# Revit family: Domotics-DomesticRanges-GEWISS-27COMBI_SYSTEM-IP40_1P_2P_3P_4P
name_source: partatom
category: Apparecchi elettrici
revit_build: Autodesk Revit 2016 (Build: 20161004_0715(x64)
units: mm (PartAtom-declared; Revit-internal decimal feet)

## family parameters
Condiviso = No
Host = Superficie
Mantenere orientamento annotazione = Sì
Numero OmniClass = 23.80.30.14.24
Punto di calcolo locali = No
Quota connettore circolare = Usa diametro
Taglio con vuoti quando caricato = Sì
Tipo di parte = Normale
Titolo OmniClass = Junction Boxes

## types (1)
- Domotics-DomesticRanges-GEWISS-27COMBI_SYSTEM-IP40_1P_2P_3P_4P
    Bidimensionale = bidimensionale system contenitori IP40 : 4P
    Catalogue = DOMOTICS
    Catalogue Range = 27COMBI
    Characteristics = Halogen free
    Colour = Grey RAL 7035
    Description: = 4 gang
    Descrizione = 4(4X1) GANG HORIZ.ENCLOSURE IP40
    Dimensions LxHxD (mm) = 132x82x55
    EAN code = 8011564055278
    Electrocod = 0212
    Glow Wire Test = 650°C
    IDF = dc894d2b-05e3-482b-a6df-8dd39df67a35
    IDT = 82b015b6-7012-4d9f-be0c-4a0004cde615
    IP degree = IP40
    Immagine tipo = GW27004.jpg
    Installation temperature = -25 +60 °C
    Insulation class = II
    Larghezza foro = 92 mm  [stored 0.301837 ft]
    Larghezza scatola = 132 mm  [stored 0.433071 ft]
    Lid screws = Corrosion-resistant steel
    Modello = GW27004
    No. knockout holes Ã˜ 23 = 8
    No. knockout holes Ã˜23 = 8 on sides / 1 on the bottom
    Outer dim. LxHxD (mm) = 132x82x55
    Produttore = GEWISS S.p.A.
    Prospetto di default = 1219 mm
    SCATOLA = GEWISS GRIGIO
    SEO = Enclosure
    Shock resistance = IK07
    Standard; = EN 60670-1
    Technical sheet = https://www.gewiss.com
    Thermo-pressure with ball = 70
    Tipo = SYSTEM CONTENITORI IP40_BASE : GW27004 - 4 posti
    Torque screws tightening = 0,8NM
    Type of knockout holes = Removable with tool
    URL = https://www.gewiss.com
    Version file RFA = 19.4

note: source unit labels omitted for Thermo-pressure with ball — the stored unit's dimension contradicts the parameter name (converter mislabeling)

note: [stored X ft] marks values corroborated as IEEE doubles in the binary element streams (Revit-internal decimal feet)

## geometry (parser evidence)
native form markers: Blend x2
no freeform markers — native parametric forms only
